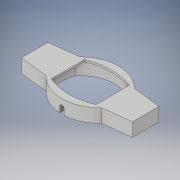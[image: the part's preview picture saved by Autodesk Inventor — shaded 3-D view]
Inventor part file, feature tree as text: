
AUTODESK INVENTOR PART (.ipt)
format: ipt  version: 2019 (Build 230136000, 136)  size: 1,514,496 bytes
history: native  units: mm
features: sketch x9, extrude x5, other x5, projected_geometry x5, revolve x2, plane x1, fillet x1
ambient origin geometry x8: Origin, YZ Plane, XZ Plane, XY Plane, X Axis, Y Axis, Z Axis, Center Point
bodies: Volumenkörper1 (feature_tree)
feature tree (28):
  sketch  "Skizze1"  dims[d9=15.2mm d12=13.036764mm]
  sketch  "Skizze2"  dims[d38=15.2mm d47=8.714705mm]
  sketch  "Skizze3"  dims[d49=8.715mm d57=15.197209mm]
  extrude  "Extrusion1"  Depth=13.036764mm
  extrude  "Extrusion3"  Depth=8.714705mm
  extrude  "Extrusion4"  Depth=15.197209mm
  extrude  "Extrusion5"  Depth=11.912488mm
  plane  "Arbeitsebene3"
  other  "Trennen3"
  fillet  "Rundung5"  Radius=1.0mm
  extrude  "Extrusion6"  Depth=3.1mm
  revolve  "Umdrehung2"
  revolve  "Umdrehung3"
  other  "Bild2"
  other  "Bild3"
  other  "Bild4"
  sketch  "Skizze4"  dims[d58=15.197209mm d59=11.912488mm d60=1.0mm]
  sketch  "Skizze8"  dims[d61=3.1mm d62=0.0mm d67=8.853mm]
  projected_geometry  "Projizierte Kontur4"
  sketch  "Skizze9"  dims[d69=0.0mm]
  projected_geometry  "Projizierte Kontur5"
  sketch  "Skizze10"  dims[d70=8.853mm]
  projected_geometry  "Projizierte Kontur6"
  projected_geometry  "Projizierte Kontur7"
  sketch  "Skizze12"  dims[d73=0.5mm d74=0.0mm]
  projected_geometry  "Projizierte Kontur8"
  sketch  "Skizze13"  dims[d75=0.6mm d76=90.0deg d77=1.55mm d78=0.5mm d79=0.0mm d80=4.4265mm d81=4.4265mm d82=8.798192mm d83=8.798192mm d84=3.531987mm d85=3.531987mm d86=4.8mm d87=0.0mm d91=1.745329mm d92=1.0mm d95=2.3mm d96=0.0mm d98=-2.268928mm d102=1.0mm d103=1.745329mm d104=1.0mm d105=1.0mm]
  other  "Arbeitsachse4"
